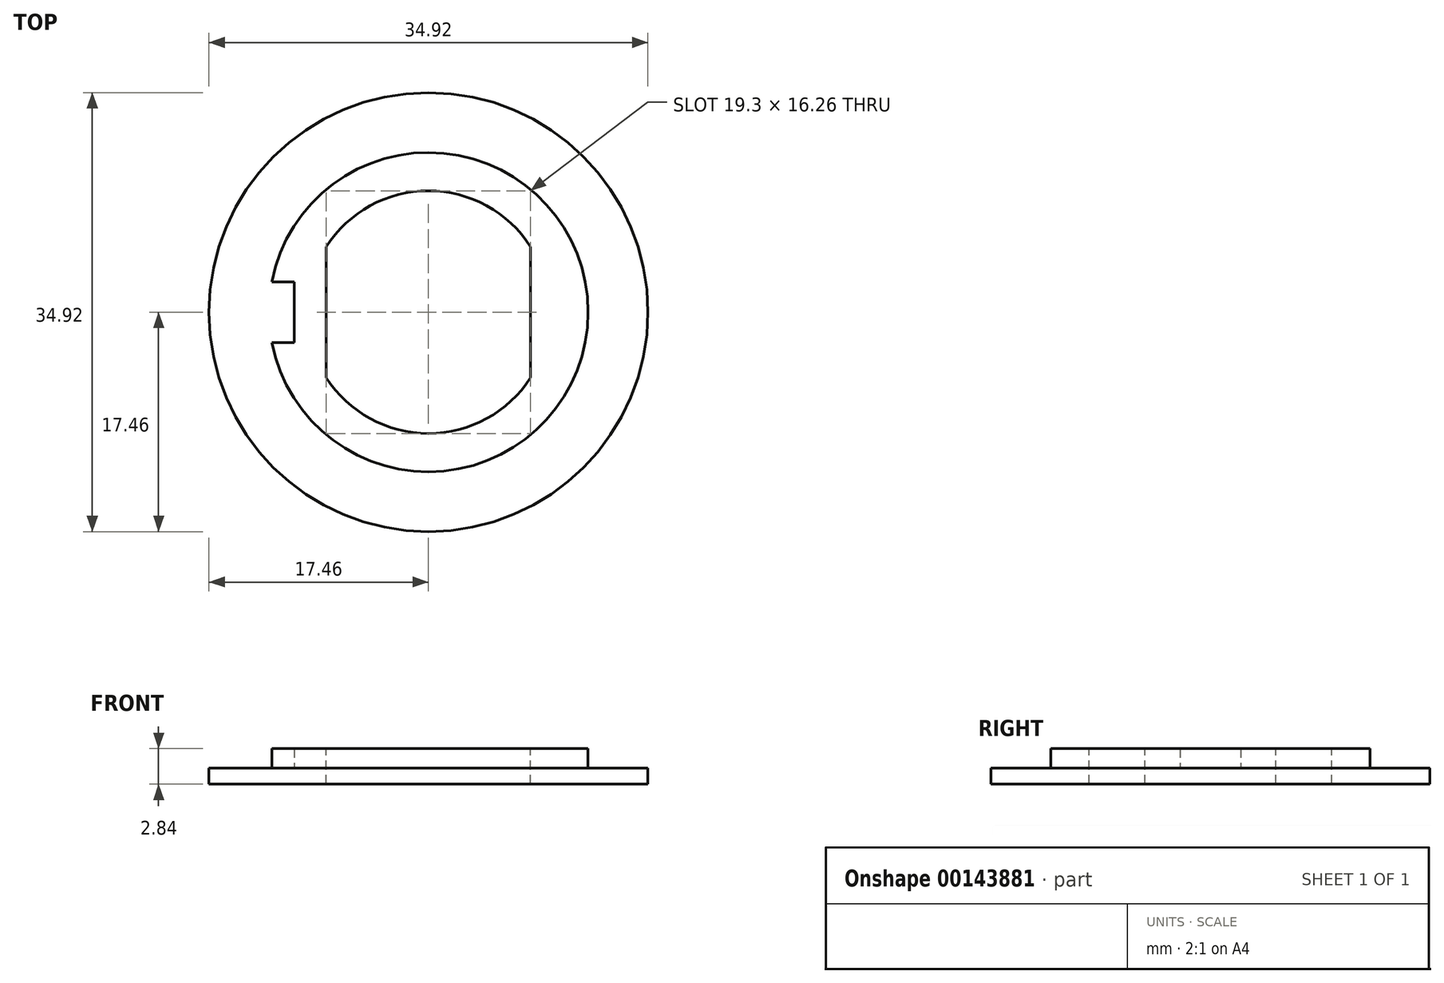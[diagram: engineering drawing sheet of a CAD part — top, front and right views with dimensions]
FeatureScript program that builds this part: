
annotation { "Feature Type Name" : "Feature", "Feature Type Description" : "" }
export const myFeature = defineFeature(function(context is Context, id is Id, definition is map)
    precondition{}
    {
        {
            var Q0;
            Q0=qCreatedBy(makeId("Top.planeOp"),FACE);
            var sketch = newSketch(context, id + "F0", { "sketchPlane" : qUnion([Q0])});
            skCircle(sketch, "E0", {"center": v(0, 0) * mm, "radius": 17.46 * mm});
            skSolve(sketch);
        }
        {
            var Q0;
            Q0 = qSketchRegion(id + "F0", true);
            extrude(context, id + "F1", {"entities" : qUnion([Q0]), "depth" : 1.27 * mm});
        }
        {
            var Q0;
            Q0=makeQuery(id+"F1.opExtrude","CAP_FACE",FACE,{"disambiguationData":[OSD([sQuery(id+"F0.wireOp",EDGE,"E0")])],"isStart":false});
            var sketch = newSketch(context, id + "F2", { "sketchPlane" : qUnion([Q0])});
            skArc(sketch, "E1", {"start": v(-12.47, -2.41) * mm, "mid": v(12.7, 0) * mm, "end": v(-12.47, 2.41) * mm});
            skLineSegment(sketch, "E2", {"start": v(0, 0) * mm, "end": v(-30.55, 0) * mm, "construction": true});
            skLineSegment(sketch, "E3", {"start": v(-12.7, 2.41) * mm, "end": v(-10.67, 2.41) * mm});
            skLineSegment(sketch, "E4", {"start": v(-12.47, -2.41) * mm, "end": v(-10.67, -2.41) * mm});
            skLineSegment(sketch, "E5", {"start": v(-12.7, 0) * mm, "end": v(-12.7, 14.04) * mm, "construction": true});
            skLineSegment(sketch, "E6", {"start": v(-10.67, 2.41) * mm, "end": v(-10.67, -2.41) * mm});
            skSolve(sketch);
        }
        {
            var Q0;
            {var subQ0=sQuery(id+"F2.wireOp",EDGE,"E1");Q0=makeQuery(id+"F2.imprint","IMPRINT",FACE,{"disambiguationData":[TD([[makeQuery(id+"F2.imprint","IMPRINT",EDGE,{"derivedFrom":subQ0}),1.0]])]});}
            extrude(context, id + "F3", {"entities" : qUnion([Q0]), "operationType" : NewBodyOperationType.ADD, "depth" : 1.57 * mm});
        }
        {
            var Q0;
            Q0=makeQuery(id+"F3.opExtrude","CAP_FACE",FACE,{"disambiguationData":[OSD([sQuery(id+"F2.wireOp",EDGE,"E1"),sQuery(id+"F2.wireOp",EDGE,"E3"),sQuery(id+"F2.wireOp",EDGE,"E4"),sQuery(id+"F2.wireOp",EDGE,"E6")])],"isStart":false});
            var sketch = newSketch(context, id + "F4", { "sketchPlane" : qUnion([Q0])});
            skArc(sketch, "E7", {"start": v(-8.13, -5.2) * mm, "mid": v(0, -9.65) * mm, "end": v(8.13, -5.2) * mm});
            skLineSegment(sketch, "E8", {"start": v(-8.13, 5.2) * mm, "end": v(-8.13, -5.2) * mm});
            skLineSegment(sketch, "E9", {"start": v(8.13, 5.2) * mm, "end": v(8.13, -5.2) * mm});
            skArc(sketch, "E10.trimOffspring", {"start": v(8.13, 5.2) * mm, "mid": v(0, 9.65) * mm, "end": v(-8.13, 5.2) * mm});
            skSolve(sketch);
        }
        {
            var Q0;
            Q0 = qSketchRegion(id + "F4", true);
            extrude(context, id + "F5", {"entities" : qUnion([Q0]), "operationType" : NewBodyOperationType.REMOVE, "endBound" : BoundingType.THROUGH_ALL, "oppositeDirection" : true, "depth" : 25.4 * mm});
        }
    });
